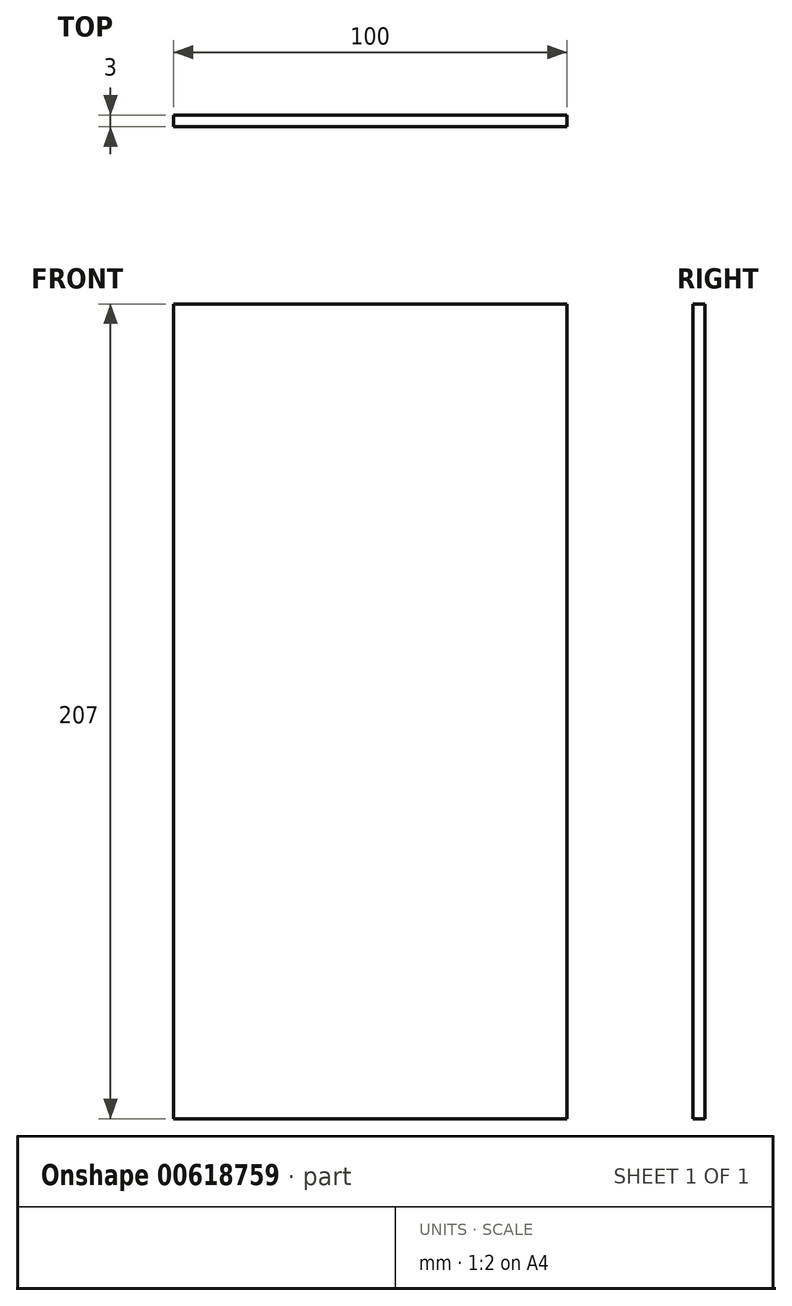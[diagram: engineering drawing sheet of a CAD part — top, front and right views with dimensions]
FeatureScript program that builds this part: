
annotation { "Feature Type Name" : "Feature", "Feature Type Description" : "" }
export const myFeature = defineFeature(function(context is Context, id is Id, definition is map)
    precondition{}
    {
        {
            var Q0;
            Q0=qCreatedBy(makeId("Front.planeOp"),FACE);
            var sketch = newSketch(context, id + "F0", { "sketchPlane" : qUnion([Q0])});
            skLineSegment(sketch, "E0.bottom", {"start": v(50, -103.5) * mm, "end": v(-50, -103.5) * mm});
            skLineSegment(sketch, "E0.top", {"start": v(50, 103.5) * mm, "end": v(-50, 103.5) * mm});
            skLineSegment(sketch, "E0.left", {"start": v(50, -103.5) * mm, "end": v(50, 103.5) * mm});
            skLineSegment(sketch, "E0.right", {"start": v(-50, -103.5) * mm, "end": v(-50, 103.5) * mm});
            skPoint(sketch, "E0.middle", {"position": v(0, 0) * mm});
            skSolve(sketch);
        }
        {
            var Q0;
            Q0 = qSketchRegion(id + "F0", true);
            extrude(context, id + "F1", {"entities" : qUnion([Q0]), "depth" : 3 * mm, "offsetDistance" : 25 * mm});
        }
    });
